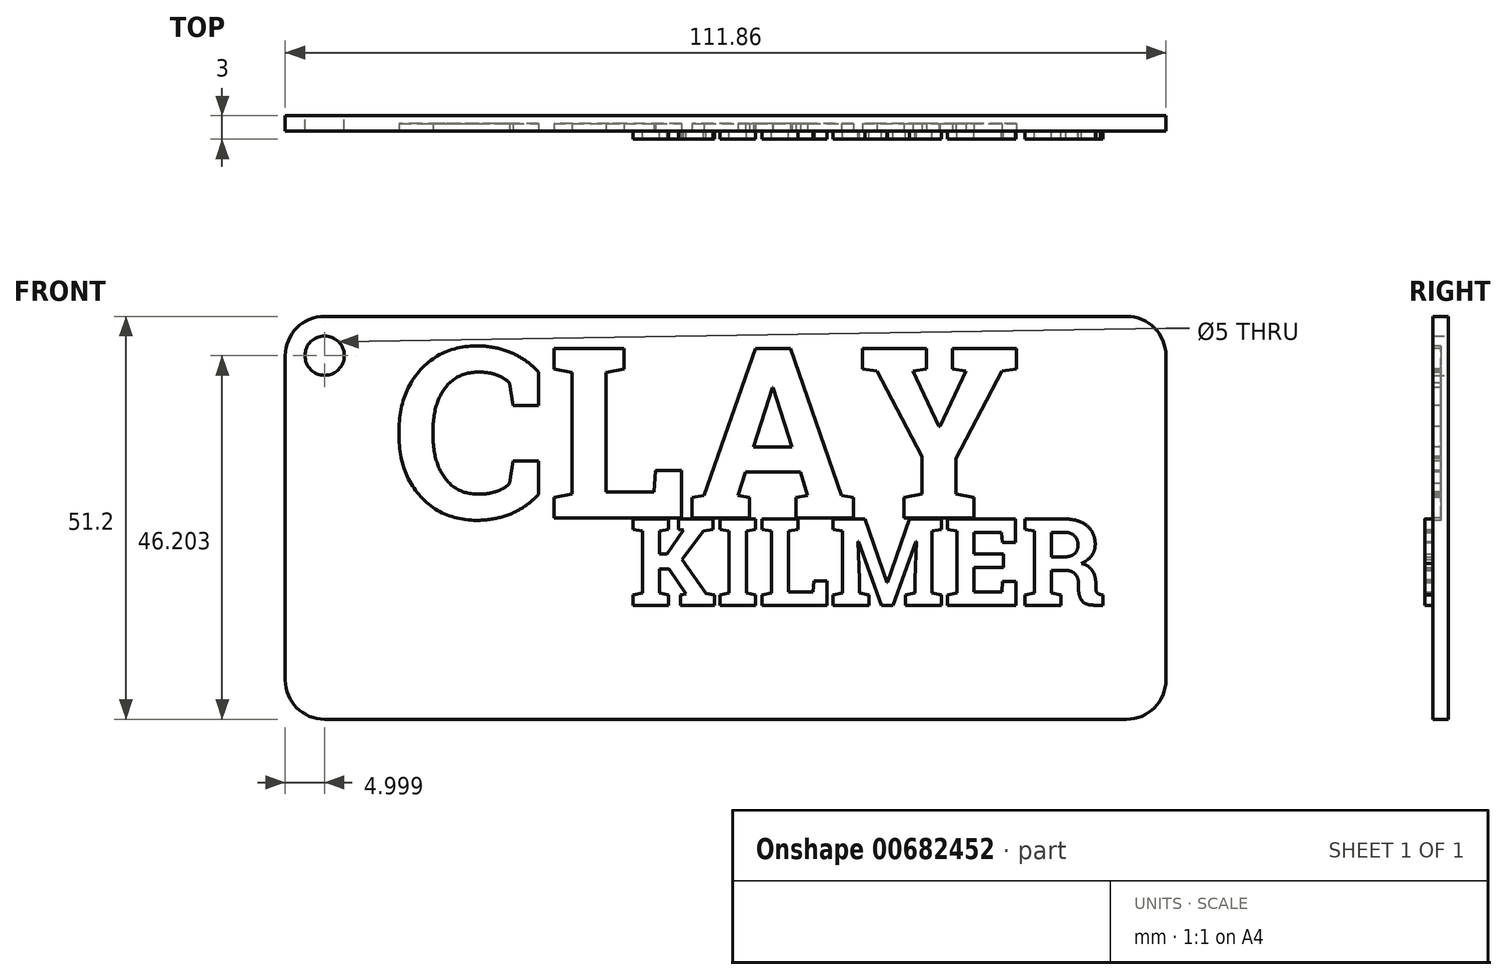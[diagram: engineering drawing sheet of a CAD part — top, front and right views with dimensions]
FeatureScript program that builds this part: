
annotation { "Feature Type Name" : "Feature", "Feature Type Description" : "" }
export const myFeature = defineFeature(function(context is Context, id is Id, definition is map)
    precondition{}
    {
        {
            var Q0;
            Q0=qCreatedBy(makeId("Front.planeOp"),FACE);
            var sketch = newSketch(context, id + "F0", { "sketchPlane" : qUnion([Q0])});
            skLineSegment(sketch, "E0.bottom", {"start": v(-50.93, 25.6) * mm, "end": v(50.93, 25.6) * mm});
            skLineSegment(sketch, "E0.top", {"start": v(-50.93, -25.6) * mm, "end": v(50.93, -25.6) * mm});
            skLineSegment(sketch, "E0.left", {"start": v(-55.93, 20.6) * mm, "end": v(-55.93, -20.6) * mm});
            skLineSegment(sketch, "E0.right", {"start": v(55.93, 20.6) * mm, "end": v(55.93, -20.6) * mm});
            skPoint(sketch, "E0.middle", {"position": v(0, 0) * mm});
            skPoint(sketch, "E1.visualSharp", {"position": v(-55.93, 25.6) * mm});
            skArc(sketch, "E1.filletArc", {"start": v(-50.93, 25.6) * mm, "mid": v(-54.47, 24.14) * mm, "end": v(-55.93, 20.6) * mm});
            skPoint(sketch, "E2.visualSharp", {"position": v(-55.93, -25.6) * mm});
            skArc(sketch, "E2.filletArc", {"start": v(-55.93, -20.6) * mm, "mid": v(-54.47, -24.14) * mm, "end": v(-50.93, -25.6) * mm});
            skPoint(sketch, "E3.visualSharp", {"position": v(55.93, -25.6) * mm});
            skArc(sketch, "E3.filletArc", {"start": v(50.93, -25.6) * mm, "mid": v(54.47, -24.14) * mm, "end": v(55.93, -20.6) * mm});
            skPoint(sketch, "E4.visualSharp", {"position": v(55.93, 25.6) * mm});
            skArc(sketch, "E4.filletArc", {"start": v(55.93, 20.6) * mm, "mid": v(54.47, 24.14) * mm, "end": v(50.93, 25.6) * mm});
            skSolve(sketch);
        }
        {
            var Q0;
            Q0=makeQuery(id+"F0.imprint","IMPRINT",FACE,{"disambiguationData":[TD([[makeQuery(id+"F0.imprint","IMPRINT",EDGE,{"derivedFrom":sQuery(id+"F0.wireOp",EDGE,"E0.bottom")}),-1.0]])]});
            extrude(context, id + "F1", {"entities" : qUnion([Q0]), "depth" : 2 * mm, "offsetDistance" : 25 * mm});
        }
        {
            var Q0;
            Q0=makeQuery(id+"F1.opExtrude","CAP_FACE",FACE,{"disambiguationData":[OSD([sQuery(id+"F0.wireOp",EDGE,"E0.bottom"),sQuery(id+"F0.wireOp",EDGE,"E0.top"),sQuery(id+"F0.wireOp",EDGE,"E0.left"),sQuery(id+"F0.wireOp",EDGE,"E0.right"),sQuery(id+"F0.wireOp",EDGE,"E1.filletArc"),sQuery(id+"F0.wireOp",EDGE,"E2.filletArc"),sQuery(id+"F0.wireOp",EDGE,"E3.filletArc"),sQuery(id+"F0.wireOp",EDGE,"E4.filletArc")])],"isStart":false});
            var sketch = newSketch(context, id + "F2", { "sketchPlane" : qUnion([Q0])});
            skCircle(sketch, "E5", {"center": v(-50.93, 20.6) * mm, "radius": 3.8 * mm});
            skSolve(sketch);
        }
        {
            var Q0;
            Q0=sQuery(id+"F0.wireOp",VERTEX,"E1.filletArc.center");
            var Q1;
            Q1=makeQuery(id+"F1.opExtrude","SWEPT_BODY",BODY,{"disambiguationData":[OSD([sQuery(id+"F0.wireOp",EDGE,"E0.bottom"),sQuery(id+"F0.wireOp",EDGE,"E0.top"),sQuery(id+"F0.wireOp",EDGE,"E0.left"),sQuery(id+"F0.wireOp",EDGE,"E0.right"),sQuery(id+"F0.wireOp",EDGE,"E1.filletArc"),sQuery(id+"F0.wireOp",EDGE,"E2.filletArc"),sQuery(id+"F0.wireOp",EDGE,"E3.filletArc"),sQuery(id+"F0.wireOp",EDGE,"E4.filletArc")])]});
            hole(context, id + "F3", {"style" : HoleStyle.SIMPLE, "endStyle" : HoleEndStyle.THROUGH, "oppositeDirection" : true, "holeDiameter" : 5 * mm, "majorDiameter" : 5 * mm, "isTappedThrough" : true, "tappedDepth" : 12 * mm, "tapClearance" : 3, "locations" : qUnion([Q0]), "scope" : qUnion([Q1])});
        }
        {
            var Q0;
            Q0=makeQuery(id+"F2.imprint","IMPRINT",FACE,{"disambiguationData":[TD([[makeQuery(id+"F2.imprint","IMPRINT",EDGE,{"derivedFrom":sQuery(id+"F2.wireOp",EDGE,"E5")}),-1.0]])]});
            var sketch = newSketch(context, id + "F4", { "sketchPlane" : qUnion([Q0])});
            skText(sketch, "E6", { "text": "CLAY", "fontName": "RobotoSlab-Bold.ttf"});
            const initialGuessF4  = {"E6": [-0.04225, 0, 1, 0, 0.0218]};
            skSetInitialGuess(sketch, initialGuessF4);
            skSolve(sketch);
        }
        {
            var Q0;
            Q0=makeQuery(id+"F2.imprint","IMPRINT",FACE,{"disambiguationData":[TD([[makeQuery(id+"F2.imprint","IMPRINT",EDGE,{"derivedFrom":sQuery(id+"F2.wireOp",EDGE,"E5")}),-1.0]])]});
            var sketch = newSketch(context, id + "F5", { "sketchPlane" : qUnion([Q0])});
            skText(sketch, "E7", { "text": "KILMER", "fontName": "RobotoSlab-Bold.ttf"});
            const initialGuessF5  = {"E7": [-0.01217, -0.0111, 1, 0, 0.0111]};
            skSetInitialGuess(sketch, initialGuessF5);
            skSolve(sketch);
        }
        {
            var Q0;
            Q0 = qSketchRegion(id + "F5", true);
            extrude(context, id + "F6", {"entities" : qUnion([Q0]), "operationType" : NewBodyOperationType.ADD, "depth" : 1 * mm, "offsetDistance" : 25 * mm});
        }
        {
            var Q0;
            Q0 = qSketchRegion(id + "F4", true);
            extrude(context, id + "F7", {"entities" : qUnion([Q0]), "operationType" : NewBodyOperationType.REMOVE, "oppositeDirection" : true, "depth" : 1 * mm, "offsetDistance" : 25 * mm});
        }
    });
